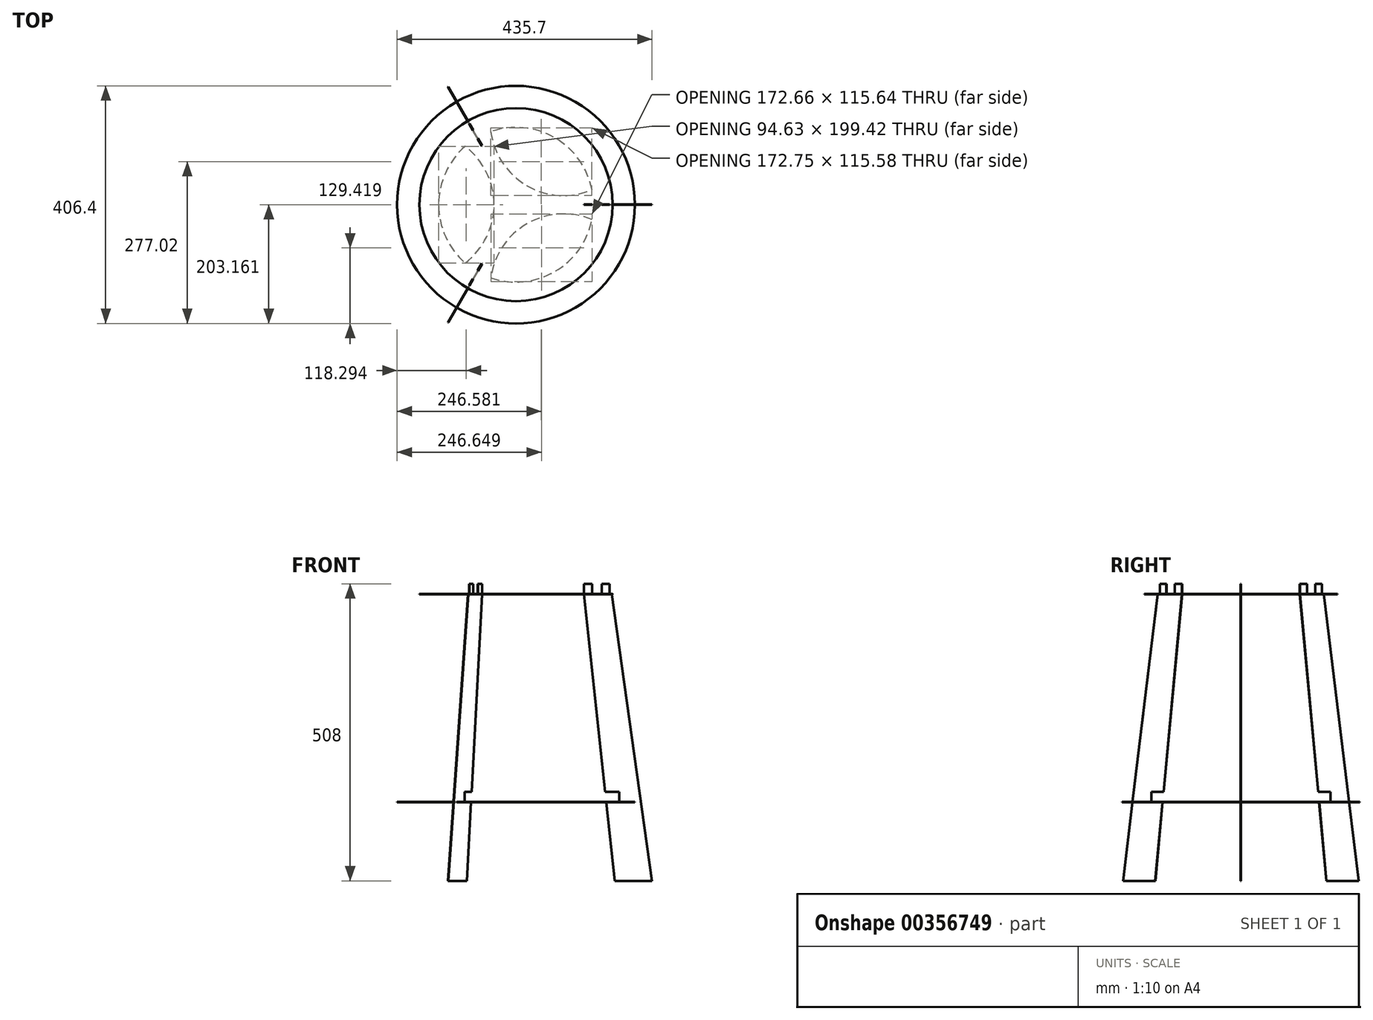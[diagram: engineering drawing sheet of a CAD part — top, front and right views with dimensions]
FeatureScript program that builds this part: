
annotation { "Feature Type Name" : "Feature", "Feature Type Description" : "" }
export const myFeature = defineFeature(function(context is Context, id is Id, definition is map)
    precondition{}
    {
        {
            assignVariable(context, id + "F0", {"name" : "ply", "anyValue" : .708});
        }
        {
            var Q0;
            Q0=qCreatedBy(makeId("Top.planeOp"),FACE);
            var sketch = newSketch(context, id + "F1", { "sketchPlane" : qUnion([Q0])});
            skCircle(sketch, "E0", {"center": v(0, 0) * mm, "radius": 165.1 * mm});
            skSolve(sketch);
        }
        {
            var Q0;
            Q0 = qSketchRegion(id + "F1", true);
            extrude(context, id + "F2", {"entities" : qUnion([Q0]), "depth" : (getVariable(context, 'ply')) * mm});
        }
        {
            var Q0;
            Q0=qCreatedBy(makeId("Top.planeOp"),FACE);
            cPlane(context, id + "F3", {"entities" : qUnion([Q0]), "cplaneType" : CPlaneType.OFFSET, "offset" : 355.6 * mm, "oppositeDirection" : true, "width" : 152.4 * mm, "height" : 152.4 * mm});
        }
        {
            var Q0;
            Q0=qCreatedBy(id+"F3.planeOp",FACE);
            var sketch = newSketch(context, id + "F4", { "sketchPlane" : qUnion([Q0])});
            skCircle(sketch, "E1", {"center": v(0, 0) * mm, "radius": 203.2 * mm});
            skSolve(sketch);
        }
        {
            var Q0;
            Q0 = qSketchRegion(id + "F4", true);
            extrude(context, id + "F5", {"entities" : qUnion([Q0]), "depth" : (getVariable(context, 'ply')) * mm});
        }
        {
            var Q0;
            Q0=qCreatedBy(makeId("Front.planeOp"),FACE);
            var sketch = newSketch(context, id + "F6", { "sketchPlane" : qUnion([Q0])});
            skLineSegment(sketch, "E2", {"start": v(0, 0) * mm, "end": v(116.3, 0) * mm, "construction": true});
            skLineSegment(sketch, "E3", {"start": v(232.5, -490.02) * mm, "end": v(168.89, -490.02) * mm});
            skLineSegment(sketch, "E4.0", {"start": v(116.3, 0) * mm, "end": v(152.53, -337.62) * mm});
            skLineSegment(sketch, "E5", {"start": v(159.67, 17.98) * mm, "end": v(146.88, 17.98) * mm});
            skLineSegment(sketch, "E6", {"start": v(116.3, 0) * mm, "end": v(116.3, 17.98) * mm});
            skLineSegment(sketch, "E7", {"start": v(152.53, -337.62) * mm, "end": v(154.95, -337.62) * mm});
            skLineSegment(sketch, "E8.trimOffspring", {"start": v(154.46, -355.6) * mm, "end": v(168.89, -490.02) * mm});
            skLineSegment(sketch, "E9", {"start": v(116.3, 17.98) * mm, "end": v(130.37, 17.98) * mm});
            skLineSegment(sketch, "E10", {"start": v(130.37, 17.98) * mm, "end": v(130.37, 0) * mm});
            skLineSegment(sketch, "E11", {"start": v(130.37, 0) * mm, "end": v(146.88, 0) * mm});
            skLineSegment(sketch, "E12", {"start": v(146.88, 0) * mm, "end": v(146.88, 17.98) * mm});
            skLineSegment(sketch, "E13", {"start": v(146.88, 17.98) * mm, "end": v(159.67, 17.98) * mm});
            skLineSegment(sketch, "E14", {"start": v(159.67, 17.98) * mm, "end": v(159.67, 0) * mm});
            skLineSegment(sketch, "E15.trimOffspring", {"start": v(130.37, 17.98) * mm, "end": v(116.3, 17.98) * mm});
            skLineSegment(sketch, "E16.trimOffspring", {"start": v(159.67, 0) * mm, "end": v(163.63, 0) * mm, "construction": true});
            skLineSegment(sketch, "E17.trimOffspring", {"start": v(130.37, 0) * mm, "end": v(146.88, 0) * mm, "construction": true});
            skLineSegment(sketch, "E18", {"start": v(154.46, -355.6) * mm, "end": v(176.69, -355.6) * mm});
            skLineSegment(sketch, "E19", {"start": v(176.69, -355.6) * mm, "end": v(176.69, -337.62) * mm});
            skLineSegment(sketch, "E20", {"start": v(176.69, -337.62) * mm, "end": v(152.53, -337.62) * mm});
            skLineSegment(sketch, "E21", {"start": v(159.67, 0) * mm, "end": v(163.63, 0) * mm});
            skLineSegment(sketch, "E22", {"start": v(163.63, 0) * mm, "end": v(232.5, -490.02) * mm});
            skSolve(sketch);
        }
        {
            var Q0;
            Q0 = qSketchRegion(id + "F6", true);
            extrude(context, id + "F7", {"entities" : qUnion([Q0]), "depth" : (getVariable(context, 'ply')) * mm, "symmetric" : true});
        }
        {
            var Q0;
            Q0=qCreatedBy(makeId("Front.planeOp"),FACE);
            var sketch = newSketch(context, id + "F8", { "sketchPlane" : qUnion([Q0])});
            skLineSegment(sketch, "E23", {"start": v(0, 0) * mm, "end": v(0, 117.8) * mm});
            skSolve(sketch);
        }
        {
            var Q0;
            Q0=makeQuery(id+"F7.opExtrude","SWEPT_BODY",BODY,{"disambiguationData":[OSD([sQuery(id+"F6.wireOp",EDGE,"KBuSjYU6-w2VD-Fk23-wxU7-WmCm703e6niA"),sQuery(id+"F6.wireOp",EDGE,"E3"),sQuery(id+"F6.wireOp",EDGE,"E4.0"),sQuery(id+"F6.wireOp",EDGE,"E5"),sQuery(id+"F6.wireOp",EDGE,"E6")])]});
            var Q1;
            Q1=sQuery(id+"F8.wireOp",EDGE,"E23");
            circularPattern(context, id + "F9", {"entities" : qUnion([Q0]), "axis" : qUnion([Q1]), "angle" : 360 * degree, "instanceCount" : 3, "equalSpace" : true});
        }
        {
            var Q0;
            Q0=makeQuery(id+"F7.opExtrude","SWEPT_BODY",BODY,{"disambiguationData":[OSD([sQuery(id+"F6.wireOp",EDGE,"KBuSjYU6-w2VD-Fk23-wxU7-WmCm703e6niA"),sQuery(id+"F6.wireOp",EDGE,"E3"),sQuery(id+"F6.wireOp",EDGE,"E4.0"),sQuery(id+"F6.wireOp",EDGE,"E5"),sQuery(id+"F6.wireOp",EDGE,"E6")])]});
            var Q1;
            Q1=makeQuery(id+"F9.opPattern","COPY",BODY,{"derivedFrom":makeQuery(id+"F7.opExtrude","SWEPT_BODY",BODY,{"disambiguationData":[OSD([sQuery(id+"F6.wireOp",EDGE,"KBuSjYU6-w2VD-Fk23-wxU7-WmCm703e6niA"),sQuery(id+"F6.wireOp",EDGE,"E3"),sQuery(id+"F6.wireOp",EDGE,"E4.0"),sQuery(id+"F6.wireOp",EDGE,"E5"),sQuery(id+"F6.wireOp",EDGE,"E6")])]}),"instanceName":"3"});
            var Q2;
            Q2=makeQuery(id+"F9.opPattern","COPY",BODY,{"derivedFrom":makeQuery(id+"F7.opExtrude","SWEPT_BODY",BODY,{"disambiguationData":[OSD([sQuery(id+"F6.wireOp",EDGE,"KBuSjYU6-w2VD-Fk23-wxU7-WmCm703e6niA"),sQuery(id+"F6.wireOp",EDGE,"E3"),sQuery(id+"F6.wireOp",EDGE,"E4.0"),sQuery(id+"F6.wireOp",EDGE,"E5"),sQuery(id+"F6.wireOp",EDGE,"E6")])]}),"instanceName":"2"});
            var Q3;
            Q3=makeQuery(id+"F9.opPattern","COPY",BODY,{"derivedFrom":makeQuery(id+"F7.opExtrude","SWEPT_BODY",BODY,{"disambiguationData":[OSD([sQuery(id+"F6.wireOp",EDGE,"KBuSjYU6-w2VD-Fk23-wxU7-WmCm703e6niA"),sQuery(id+"F6.wireOp",EDGE,"E3"),sQuery(id+"F6.wireOp",EDGE,"E4.0"),sQuery(id+"F6.wireOp",EDGE,"E5"),sQuery(id+"F6.wireOp",EDGE,"E6")])]}),"instanceName":"1"});
            var Q4;
            Q4=makeQuery(id+"F2.opExtrude","SWEPT_BODY",BODY,{"disambiguationData":[OSD([sQuery(id+"F1.wireOp",EDGE,"E0")])]});
            var Q5;
            Q5=makeQuery(id+"F5.opExtrude","SWEPT_BODY",BODY,{"disambiguationData":[OSD([sQuery(id+"F4.wireOp",EDGE,"E1")])]});
            booleanBodies(context, id + "F10", {"operationType" : BooleanOperationType.SUBTRACTION, "tools" : qUnion([Q0, Q1, Q2, Q3]), "targets" : qUnion([Q4, Q5]), "keepTools" : true});
        }
        {
            var Q0;
            Q0=makeQuery(id+"F5.opExtrude","CAP_FACE",FACE,{"disambiguationData":[OSD([sQuery(id+"F4.wireOp",EDGE,"E1")])],"isStart":false});
            var sketch = newSketch(context, id + "F11", { "sketchPlane" : qUnion([Q0])});
            skCircle(sketch, "E24", {"center": v(0, 0) * mm, "radius": 132.22 * mm});
            skLineSegment(sketch, "E25", {"start": v(0, 0) * mm, "end": v(132.22, 0) * mm});
            skLineSegment(sketch, "E26.1.0", {"start": v(0, 0) * mm, "end": v(-66.1, 114.5) * mm});
            skLineSegment(sketch, "E26.2.0", {"start": v(0, 0) * mm, "end": v(-66.1, -114.5) * mm});
            skArc(sketch, "E27", {"start": v(-43, 125.03) * mm, "mid": v(18.78, 32.56) * mm, "end": v(129.76, 25.4) * mm});
            skArc(sketch, "E28.1.0", {"start": v(-86.79, -99.75) * mm, "mid": v(-37.6, -0.02) * mm, "end": v(-86.88, 99.67) * mm});
            skArc(sketch, "E28.2.0", {"start": v(129.78, -25.28) * mm, "mid": v(18.81, -32.55) * mm, "end": v(-42.88, -125.07) * mm});
            skSolve(sketch);
        }
        {
            var Q0;
            {var subQ0=sQuery(id+"F11.wireOp",EDGE,"E27");Q0=makeQuery(id+"F11.imprint","IMPRINT",FACE,{"disambiguationData":[TD([[makeQuery(id+"F11.imprint","IMPRINT",EDGE,{"derivedFrom":subQ0}),1.0]])]});}
            var Q1;
            {var subQ0=sQuery(id+"F11.wireOp",EDGE,"E28.2.0");Q1=makeQuery(id+"F11.imprint","IMPRINT",FACE,{"disambiguationData":[TD([[makeQuery(id+"F11.imprint","IMPRINT",EDGE,{"derivedFrom":subQ0}),1.0]])]});}
            var Q2;
            {var subQ0=sQuery(id+"F11.wireOp",EDGE,"E28.1.0");Q2=makeQuery(id+"F11.imprint","IMPRINT",FACE,{"disambiguationData":[TD([[makeQuery(id+"F11.imprint","IMPRINT",EDGE,{"derivedFrom":subQ0}),1.0]])]});}
            extrude(context, id + "F12", {"entities" : qUnion([Q0, Q1, Q2]), "operationType" : NewBodyOperationType.REMOVE, "endBound" : BoundingType.UP_TO_NEXT, "oppositeDirection" : true, "depth" : 25.4 * mm});
        }
    });
